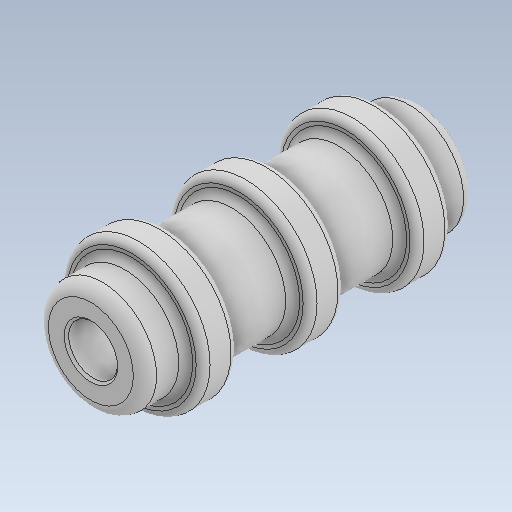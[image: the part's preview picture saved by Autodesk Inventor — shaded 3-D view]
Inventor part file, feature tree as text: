
AUTODESK INVENTOR PART (.ipt)
format: ipt  version: 2020 (Build 240168000, 168)  size: 259,072 bytes
history: native  units: in
note: dims shown in document units (in); Inventor stores cm internally (conversion verified against a paired STEP export)
features: chamfer x1
ambient origin geometry x8: Origin, YZ Plane, XZ Plane, XY Plane, X Axis, Y Axis, Z Axis, Center Point
bodies: Solid1 (feature_tree)
feature tree (1):
  chamfer  "Chamfer1"  [1 undecoded]
note: 1 required parameter value undecoded (feature->parameter linkage not recoverable at this tier; creation-order binding heuristic only, values carry confidence <= 0.55)
